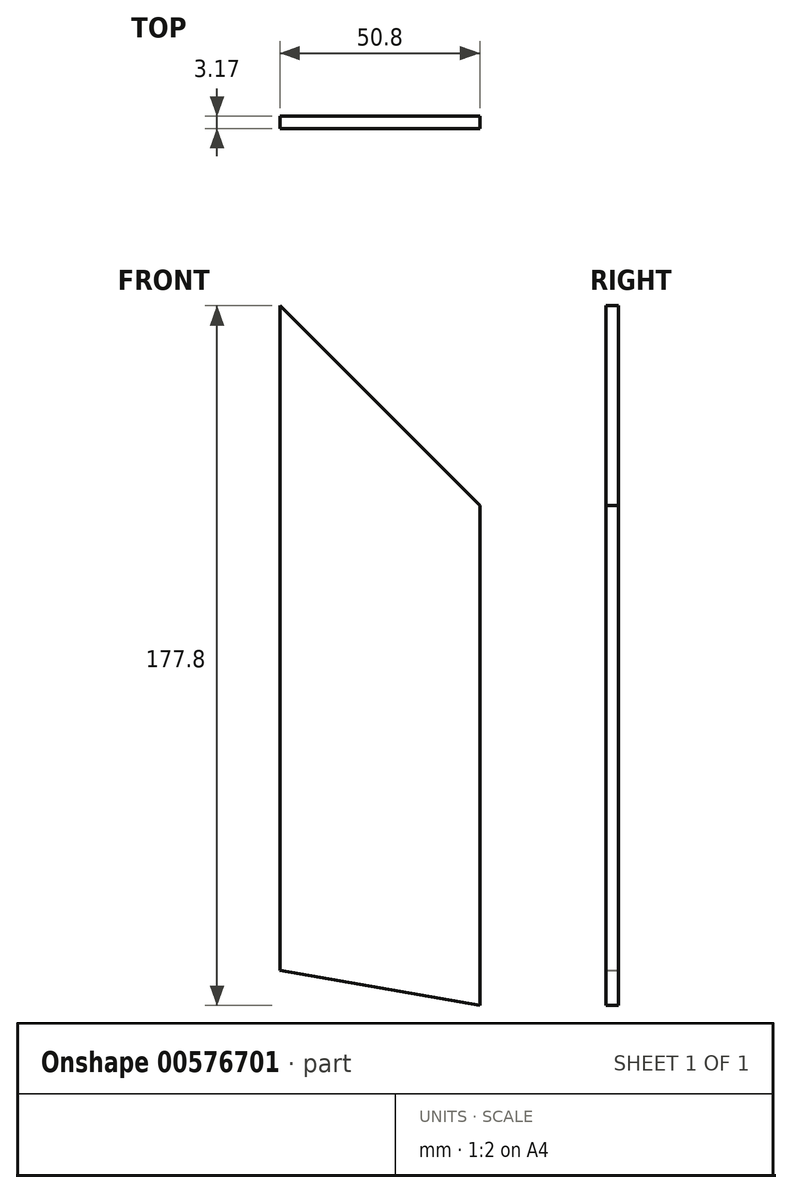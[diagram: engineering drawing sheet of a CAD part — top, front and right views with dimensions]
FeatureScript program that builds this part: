
annotation { "Feature Type Name" : "Feature", "Feature Type Description" : "" }
export const myFeature = defineFeature(function(context is Context, id is Id, definition is map)
    precondition{}
    {
        {
            var Q0;
            Q0=qCreatedBy(makeId("Front.planeOp"),FACE);
            var sketch = newSketch(context, id + "F0", { "sketchPlane" : qUnion([Q0])});
            skLineSegment(sketch, "E0.left", {"start": v(25.4, 38.1) * mm, "end": v(25.4, -88.9) * mm});
            skLineSegment(sketch, "E0.right", {"start": v(-25.4, 88.9) * mm, "end": v(-25.4, -79.94) * mm});
            skPoint(sketch, "E0.middle", {"position": v(0, 0) * mm});
            skLineSegment(sketch, "E1", {"start": v(25.4, 38.1) * mm, "end": v(-25.4, 88.9) * mm});
            skLineSegment(sketch, "E2", {"start": v(25.4, -88.9) * mm, "end": v(-25.4, -79.94) * mm});
            skPoint(sketch, "E3.orphan", {"position": v(25.4, 115.56) * mm});
            skPoint(sketch, "E4.orphan", {"position": v(-25.4, -115.56) * mm});
            skSolve(sketch);
        }
        {
            var Q0;
            Q0 = qSketchRegion(id + "F0", true);
            extrude(context, id + "F1", {"entities" : qUnion([Q0]), "depth" : 3.17 * mm, "offsetDistance" : 25.4 * mm});
        }
    });
